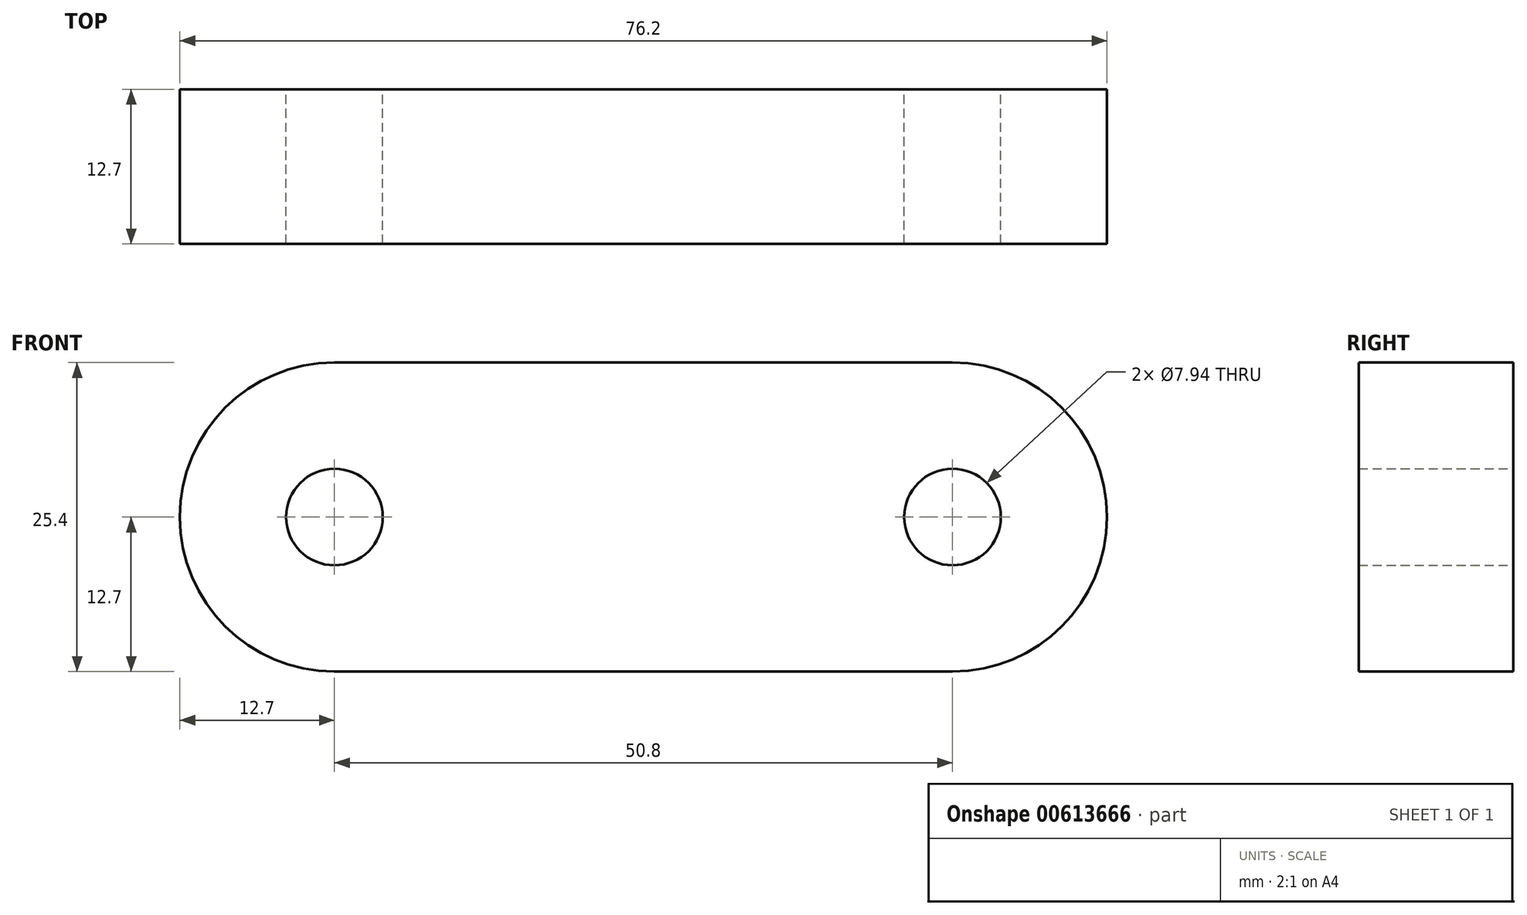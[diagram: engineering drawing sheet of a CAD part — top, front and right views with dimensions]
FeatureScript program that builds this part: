
annotation { "Feature Type Name" : "Feature", "Feature Type Description" : "" }
export const myFeature = defineFeature(function(context is Context, id is Id, definition is map)
    precondition{}
    {
        {
            var Q0;
            Q0=qCreatedBy(makeId("Front.planeOp"),FACE);
            var sketch = newSketch(context, id + "F0", { "sketchPlane" : qUnion([Q0])});
            skLineSegment(sketch, "E0.bottom", {"start": v(25.4, -12.7) * mm, "end": v(-25.4, -12.7) * mm});
            skLineSegment(sketch, "E0.top", {"start": v(25.4, 12.7) * mm, "end": v(-25.4, 12.7) * mm});
            skLineSegment(sketch, "E0.left", {"start": v(25.4, -12.7) * mm, "end": v(25.4, 12.7) * mm});
            skLineSegment(sketch, "E0.right", {"start": v(-25.4, -12.7) * mm, "end": v(-25.4, 12.7) * mm});
            skPoint(sketch, "E0.middle", {"position": v(0, 0) * mm});
            skArc(sketch, "E1", {"start": v(-25.4, 12.7) * mm, "mid": v(-38.1, 0) * mm, "end": v(-25.4, -12.7) * mm});
            skArc(sketch, "E2", {"start": v(25.4, -12.7) * mm, "mid": v(38.1, 0) * mm, "end": v(25.4, 12.7) * mm});
            skCircle(sketch, "E3", {"center": v(25.4, 0) * mm, "radius": 3.97 * mm});
            skCircle(sketch, "E4", {"center": v(-25.4, 0) * mm, "radius": 3.97 * mm});
            skSolve(sketch);
        }
        {
            var Q0;
            Q0 = qSketchRegion(id + "F0", true);
            extrude(context, id + "F1", {"entities" : qUnion([Q0]), "depth" : 12.7 * mm, "offsetDistance" : 25.4 * mm});
        }
    });
